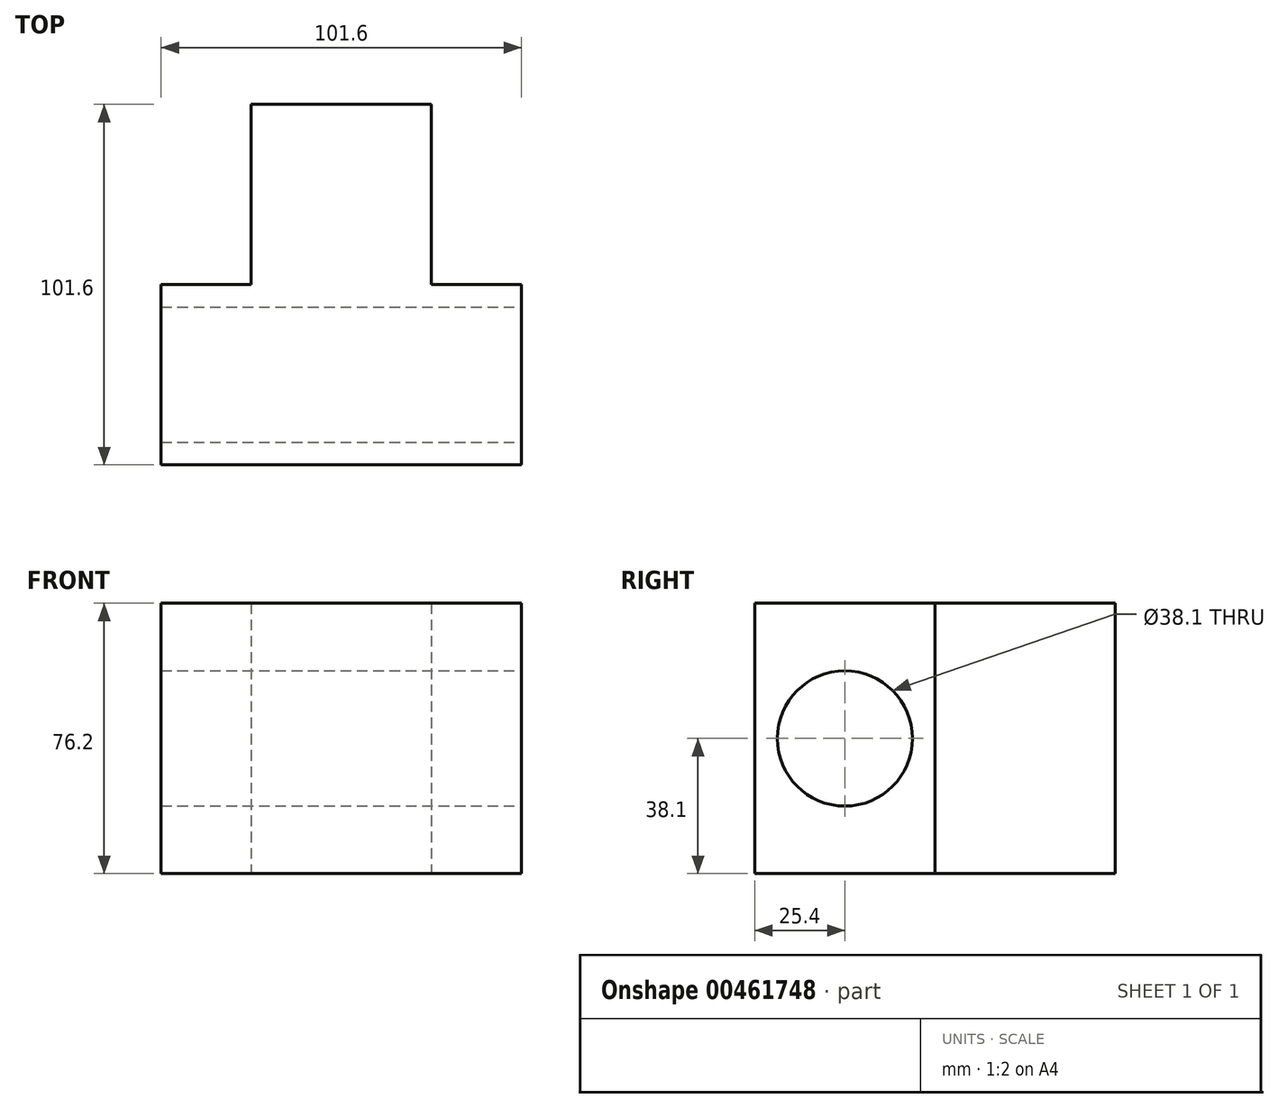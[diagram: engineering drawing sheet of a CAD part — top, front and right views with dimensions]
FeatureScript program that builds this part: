
annotation { "Feature Type Name" : "Feature", "Feature Type Description" : "" }
export const myFeature = defineFeature(function(context is Context, id is Id, definition is map)
    precondition{}
    {
        {
            var Q0;
            Q0=qCreatedBy(makeId("Top.planeOp"),FACE);
            var sketch = newSketch(context, id + "F0", { "sketchPlane" : qUnion([Q0])});
            skLineSegment(sketch, "E0.bottom", {"start": v(50.8, -25.4) * mm, "end": v(-50.8, -25.4) * mm});
            skLineSegment(sketch, "E0.top", {"start": v(50.8, 25.4) * mm, "end": v(-50.8, 25.4) * mm});
            skLineSegment(sketch, "E0.left", {"start": v(50.8, -25.4) * mm, "end": v(50.8, 25.4) * mm});
            skLineSegment(sketch, "E0.right", {"start": v(-50.8, -25.4) * mm, "end": v(-50.8, 25.4) * mm});
            skPoint(sketch, "E0.middle", {"position": v(0, 0) * mm});
            skLineSegment(sketch, "E1", {"start": v(0, 0) * mm, "end": v(0, 50.8) * mm});
            skPoint(sketch, "E1.endSnap0", {"position": v(0, 25.4) * mm});
            skLineSegment(sketch, "E2.bottom", {"start": v(25.4, 25.4) * mm, "end": v(-25.4, 25.4) * mm});
            skLineSegment(sketch, "E2.top", {"start": v(25.4, 76.2) * mm, "end": v(-25.4, 76.2) * mm});
            skLineSegment(sketch, "E2.left", {"start": v(25.4, 25.4) * mm, "end": v(25.4, 76.2) * mm});
            skLineSegment(sketch, "E2.right", {"start": v(-25.4, 25.4) * mm, "end": v(-25.4, 76.2) * mm});
            skPoint(sketch, "E2.middle", {"position": v(0, 50.8) * mm});
            skSolve(sketch);
        }
        {
            var Q0;
            Q0 = qSketchRegion(id + "F0", true);
            extrude(context, id + "F1", {"entities" : qUnion([Q0]), "endBound" : BoundingType.SYMMETRIC, "depth" : 76.2 * mm});
        }
        {
            var Q0;
            Q0=makeQuery(id+"F1.opExtrude","SWEPT_FACE",FACE,{"disambiguationData":[OSD([sQuery(id+"F0.wireOp",EDGE,"E0.left")])]});
            var sketch = newSketch(context, id + "F2", { "sketchPlane" : qUnion([Q0])});
            skCircle(sketch, "E3", {"center": v(0, 0) * mm, "radius": 19.05 * mm});
            skSolve(sketch);
        }
        {
            var Q0;
            Q0=makeQuery(id+"F2.imprint","IMPRINT",FACE,{"disambiguationData":[TD([[makeQuery(id+"F2.imprint","IMPRINT",EDGE,{"derivedFrom":sQuery(id+"F2.wireOp",EDGE,"E3")}),1.0]])]});
            extrude(context, id + "F3", {"entities" : qUnion([Q0]), "operationType" : NewBodyOperationType.REMOVE, "endBound" : BoundingType.THROUGH_ALL, "oppositeDirection" : true, "depth" : 108.46 * mm});
        }
    });
